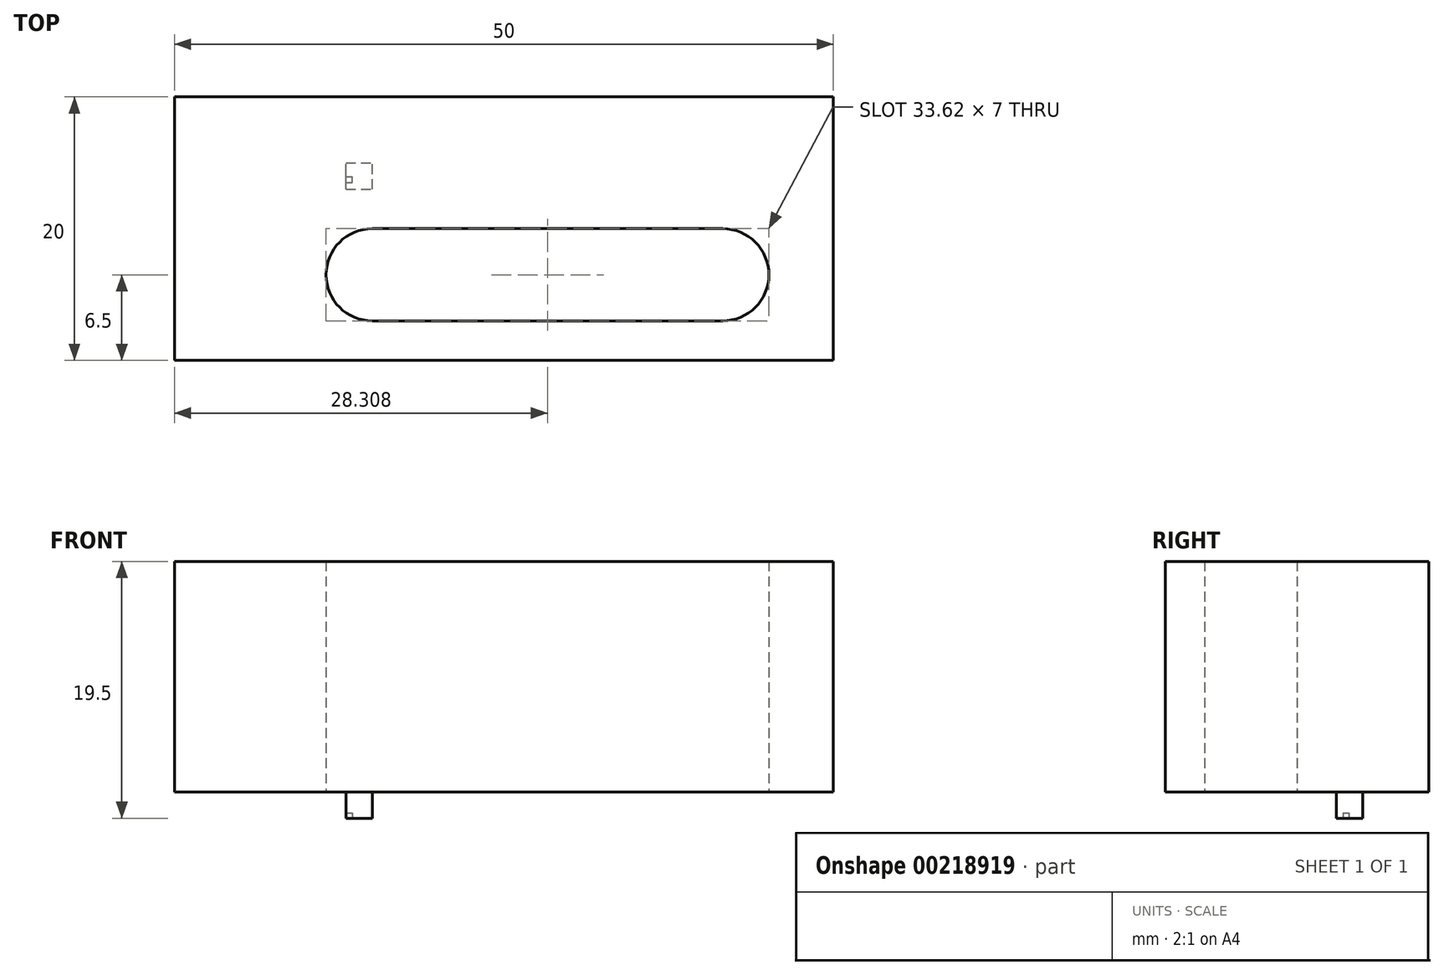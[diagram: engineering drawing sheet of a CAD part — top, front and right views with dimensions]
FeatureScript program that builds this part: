
annotation { "Feature Type Name" : "Feature", "Feature Type Description" : "" }
export const myFeature = defineFeature(function(context is Context, id is Id, definition is map)
    precondition{}
    {
        {
            var Q0;
            Q0=qCreatedBy(makeId("Top.planeOp"),FACE);
            var sketch = newSketch(context, id + "F0", { "sketchPlane" : qUnion([Q0])});
            skLineSegment(sketch, "E0.bottom", {"start": v(-15, 10) * mm, "end": v(35, 10) * mm});
            skLineSegment(sketch, "E0.top", {"start": v(-15, -10) * mm, "end": v(35, -10) * mm});
            skLineSegment(sketch, "E0.left", {"start": v(-15, 10) * mm, "end": v(-15, -10) * mm});
            skLineSegment(sketch, "E0.right", {"start": v(35, 10) * mm, "end": v(35, -10) * mm});
            skSolve(sketch);
        }
        {
            var Q0;
            Q0 = qSketchRegion(id + "F0", true);
            extrude(context, id + "F1", {"entities" : qUnion([Q0]), "depth" : 17.5 * mm, "offsetDistance" : 25 * mm});
        }
        {
            var Q0;
            Q0=qCreatedBy(makeId("Top.planeOp"),FACE);
            var sketch = newSketch(context, id + "F2", { "sketchPlane" : qUnion([Q0])});
            skLineSegment(sketch, "E1", {"start": v(0, -7) * mm, "end": v(26.62, -7) * mm});
            skArc(sketch, "E2", {"start": v(26.62, -7) * mm, "mid": v(30.12, -3.5) * mm, "end": v(26.62, 0) * mm});
            skLineSegment(sketch, "E3", {"start": v(26.62, 0) * mm, "end": v(0, 0) * mm});
            skArc(sketch, "E4", {"start": v(0, 0) * mm, "mid": v(-3.5, -3.5) * mm, "end": v(0, -7) * mm});
            skSolve(sketch);
        }
        {
            var Q0;
            Q0 = qSketchRegion(id + "F2", true);
            extrude(context, id + "F3", {"entities" : qUnion([Q0]), "operationType" : NewBodyOperationType.REMOVE, "depth" : 50 * mm, "offsetDistance" : 25 * mm});
        }
        {
            var Q0;
            Q0=makeQuery(id+"F1.opExtrude","CAP_FACE",FACE,{"disambiguationData":[OSD([sQuery(id+"F0.wireOp",EDGE,"E0.bottom"),sQuery(id+"F0.wireOp",EDGE,"E0.top"),sQuery(id+"F0.wireOp",EDGE,"E0.left"),sQuery(id+"F0.wireOp",EDGE,"E0.right")])],"isStart":true});
            var sketch = newSketch(context, id + "F4", { "sketchPlane" : qUnion([Q0])});
            skLineSegment(sketch, "E5.bottom", {"start": v(-2, -3) * mm, "end": v(0, -3) * mm});
            skLineSegment(sketch, "E5.top", {"start": v(-2, -5) * mm, "end": v(0, -5) * mm});
            skLineSegment(sketch, "E5.left", {"start": v(-2, -3) * mm, "end": v(-2, -5) * mm});
            skLineSegment(sketch, "E5.right", {"start": v(0, -3) * mm, "end": v(0, -5) * mm});
            skSolve(sketch);
        }
        {
            var Q0;
            Q0 = qSketchRegion(id + "F4", true);
            extrude(context, id + "F5", {"entities" : qUnion([Q0]), "operationType" : NewBodyOperationType.ADD, "depth" : 2 * mm, "offsetDistance" : 25 * mm});
        }
        {
            var Q0;
            Q0=makeQuery(id+"F5.opExtrude","CAP_FACE",FACE,{"disambiguationData":[OSD([sQuery(id+"F4.wireOp",EDGE,"E5.bottom"),sQuery(id+"F4.wireOp",EDGE,"E5.top"),sQuery(id+"F4.wireOp",EDGE,"E5.left"),sQuery(id+"F4.wireOp",EDGE,"E5.right")])],"isStart":false});
            var sketch = newSketch(context, id + "F6", { "sketchPlane" : qUnion([Q0])});
            skLineSegment(sketch, "E6.bottom", {"start": v(-2, -3.5) * mm, "end": v(-1.5, -3.5) * mm});
            skLineSegment(sketch, "E6.top", {"start": v(-2, -3.95) * mm, "end": v(-1.5, -3.95) * mm});
            skLineSegment(sketch, "E6.left", {"start": v(-2, -3.5) * mm, "end": v(-2, -3.95) * mm});
            skLineSegment(sketch, "E6.right", {"start": v(-1.5, -3.5) * mm, "end": v(-1.5, -3.95) * mm});
            skSolve(sketch);
        }
        {
            var Q0;
            Q0 = qSketchRegion(id + "F6", true);
            extrude(context, id + "F7", {"entities" : qUnion([Q0]), "operationType" : NewBodyOperationType.REMOVE, "oppositeDirection" : true, "depth" : 0.4 * mm, "offsetDistance" : 25 * mm});
        }
    });
